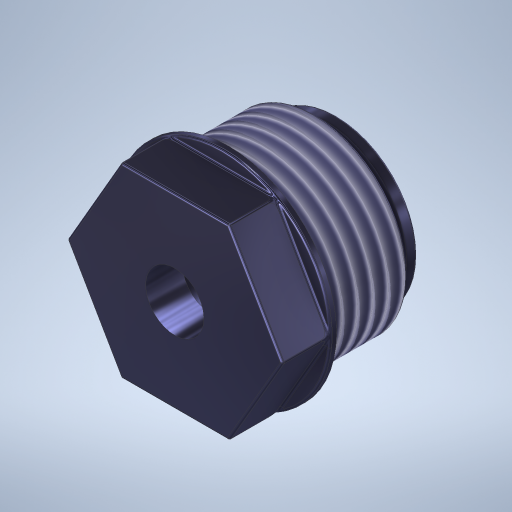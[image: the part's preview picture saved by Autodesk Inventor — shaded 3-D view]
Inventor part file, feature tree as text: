
AUTODESK INVENTOR PART (.ipt)
format: ipt  version: 2023.1 (Build 271208000, 208)  size: 544,256 bytes
history: native  units: in
note: dims shown in document units (in); Inventor stores cm internally (conversion verified against a paired STEP export)
features: sketch x6, extrude x4, fillet x2, pattern_circular x1, hole x1, revolve x1, thread x1, projected_geometry x1
ambient origin geometry x8: Origin, YZ Plane, XZ Plane, XY Plane, X Axis, Y Axis, Z Axis, Center Point
bodies: Solid1 (feature_tree)
feature tree (17):
  extrude  "Extrusion1"  Depth=0.125in TaperAngle=0.0deg
  extrude  "Extrusion2"  Depth=2.3622in TaperAngle=360.0deg
  pattern_circular  "Circular Pattern1"  [2 undecoded]
  fillet  "Fillet1"  Radius=0.05in
  extrude  "Extrusion3"  Depth=0.025in
  extrude  "Extrusion4"  Depth=0.025in
  hole  "Hole1"  [1 undecoded]
  revolve  "Revolution1"  Angle=90.0deg
  fillet  "Fillet2"  Radius=0.005in
  thread  "Thread1"  [1 undecoded]
  sketch  "Sketch1"  dims[d0=0.5in d1=0.125in d2=0.0in]
  sketch  "Sketch2"  dims[d3=0.11in d4=0.0in d5=2.3622in d6=360.0deg]
  sketch  "Sketch3"  dims[d8=0.005in]
  sketch  "Sketch4"  dims[d9=0.43in]
  sketch  "Sketch5"  dims[d10=0.25in d11=0.0in]
  sketch  "Sketch6"  dims[d12=0.25in d13=0.29in d14=0.0in d15=0.135in d16=0.224in d17=0.375in d18=0.25in d19=0.5635in d20=1.0in d21=0.8108in d22=0.05in d23=0.025in d24=0.025in d25=0.375in d26=90.0deg d27=0.005in d28=1.0in d29=0.0in]
  projected_geometry  "Project Cut Edges1"
note: 4 required parameter values undecoded (feature->parameter linkage not recoverable at this tier; creation-order binding heuristic only, values carry confidence <= 0.55)
